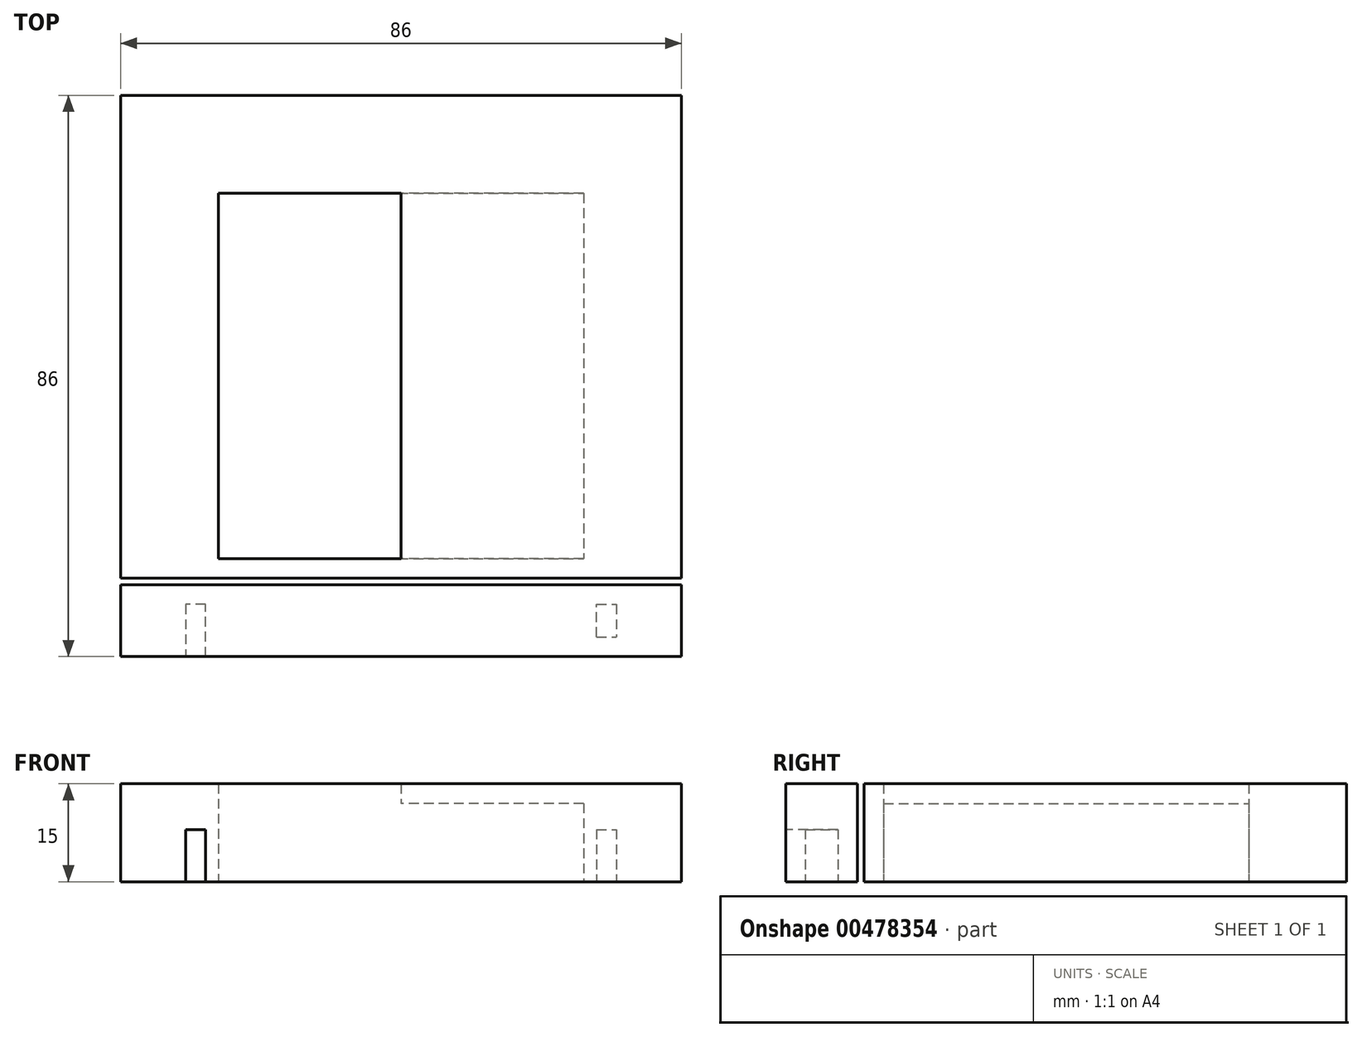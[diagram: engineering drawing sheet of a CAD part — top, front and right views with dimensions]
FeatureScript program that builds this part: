
annotation { "Feature Type Name" : "Feature", "Feature Type Description" : "" }
export const myFeature = defineFeature(function(context is Context, id is Id, definition is map)
    precondition{}
    {
        {
            var Q0;
            Q0=qCreatedBy(makeId("Top.planeOp"),FACE);
            var sketch = newSketch(context, id + "F0", { "sketchPlane" : qUnion([Q0])});
            skLineSegment(sketch, "E0", {"start": v(0, 0) * mm, "end": v(0, -43) * mm});
            skLineSegment(sketch, "E1", {"start": v(0, -43) * mm, "end": v(-43, -43) * mm});
            skLineSegment(sketch, "E2.MirrorCS", {"start": v(0, -43) * mm, "end": v(43, -43) * mm});
            skLineSegment(sketch, "E3", {"start": v(-43, -43) * mm, "end": v(-43, -32) * mm});
            skLineSegment(sketch, "E4", {"start": v(-43, -32) * mm, "end": v(0, -32) * mm});
            skLineSegment(sketch, "E5.MirrorCS", {"start": v(43, -32) * mm, "end": v(0, -32) * mm});
            skLineSegment(sketch, "E6.MirrorCS", {"start": v(43, -43) * mm, "end": v(43, -32) * mm});
            skSolve(sketch);
        }
        {
            var Q0;
            {var subQ0=sQuery(id+"F0.wireOp",EDGE,"E1");Q0=makeQuery(id+"F0.imprint","IMPRINT",FACE,{"disambiguationData":[TD([[makeQuery(id+"F0.imprint","IMPRINT",EDGE,{"derivedFrom":subQ0}),-1.0]])]});}
            var Q1;
            {var subQ0=sQuery(id+"F0.wireOp",EDGE,"E2.MirrorCS");Q1=makeQuery(id+"F0.imprint","IMPRINT",FACE,{"disambiguationData":[TD([[makeQuery(id+"F0.imprint","IMPRINT",EDGE,{"derivedFrom":subQ0}),1.0]])]});}
            extrude(context, id + "F1", {"entities" : qUnion([Q0, Q1]), "depth" : 15 * mm});
        }
        {
            var Q0;
            Q0=qCreatedBy(makeId("Top.planeOp"),FACE);
            var sketch = newSketch(context, id + "F2", { "sketchPlane" : qUnion([Q0])});
            skLineSegment(sketch, "E7", {"start": v(0, 0) * mm, "end": v(0, -43) * mm});
            skLineSegment(sketch, "E8", {"start": v(0, -43) * mm, "end": v(-30, -43) * mm});
            skLineSegment(sketch, "E9", {"start": v(-30, -43) * mm, "end": v(-30, -35) * mm});
            skLineSegment(sketch, "E10.MirrorCS", {"start": v(30, -43) * mm, "end": v(30, -35) * mm});
            skLineSegment(sketch, "E11", {"start": v(-30, -35) * mm, "end": v(-33, -35) * mm});
            skLineSegment(sketch, "E12", {"start": v(-33, -35) * mm, "end": v(-33, -43) * mm});
            skLineSegment(sketch, "E13", {"start": v(-30, -43) * mm, "end": v(-33, -43) * mm});
            skLineSegment(sketch, "E14.MirrorCS", {"start": v(33, -35) * mm, "end": v(33, -43) * mm});
            skLineSegment(sketch, "E15.MirrorCS", {"start": v(30, -43) * mm, "end": v(33, -43) * mm});
            skLineSegment(sketch, "E16.MirrorCS", {"start": v(30, -35) * mm, "end": v(33, -35) * mm});
            skLineSegment(sketch, "E17", {"start": v(-30, -43) * mm, "end": v(-30, -40) * mm});
            skLineSegment(sketch, "E18", {"start": v(-30, -40) * mm, "end": v(-33, -40) * mm});
            skLineSegment(sketch, "E19.MirrorCS", {"start": v(30, -40) * mm, "end": v(33, -40) * mm});
            skSolve(sketch);
        }
        {
            var Q0;
            Q0=makeQuery(id+"F2.imprint","IMPRINT",FACE,{"disambiguationData":[TD([[makeQuery(id+"F2.imprint","IMPRINT",EDGE,{"derivedFrom":sQuery(id+"F2.wireOp",EDGE,"E9")}),1.0]])]});
            var Q1;
            {var subQ0=sQuery(id+"F2.wireOp",EDGE,"E16.MirrorCS");Q1=makeQuery(id+"F2.imprint","IMPRINT",FACE,{"disambiguationData":[TD([[makeQuery(id+"F2.imprint","IMPRINT",EDGE,{"derivedFrom":subQ0}),-1.0]])]});}
            extrude(context, id + "F3", {"entities" : qUnion([Q0, Q1]), "operationType" : NewBodyOperationType.REMOVE, "depth" : 8 * mm});
        }
        {
            var Q0;
            Q0=qCreatedBy(makeId("Top.planeOp"),FACE);
            var sketch = newSketch(context, id + "F4", { "sketchPlane" : qUnion([Q0])});
            skLineSegment(sketch, "E20", {"start": v(0, 0) * mm, "end": v(0, 43) * mm});
            skLineSegment(sketch, "E21.bottom", {"start": v(0, 0) * mm, "end": v(-43, 0) * mm});
            skLineSegment(sketch, "E21.top", {"start": v(0, 43) * mm, "end": v(-43, 43) * mm});
            skLineSegment(sketch, "E21.right", {"start": v(-43, 0) * mm, "end": v(-43, 43) * mm});
            skLineSegment(sketch, "E22", {"start": v(-43, 0) * mm, "end": v(-43, -31) * mm});
            skLineSegment(sketch, "E23.top", {"start": v(0, -31) * mm, "end": v(-43, -31) * mm});
            skLineSegment(sketch, "E23.left", {"start": v(0, 0) * mm, "end": v(0, -31) * mm});
            skLineSegment(sketch, "E24.MirrorCS", {"start": v(0, 43) * mm, "end": v(43, 43) * mm});
            skLineSegment(sketch, "E25.MirrorCS", {"start": v(43, 0) * mm, "end": v(43, 43) * mm});
            skLineSegment(sketch, "E26.MirrorCS", {"start": v(0, -31) * mm, "end": v(43, -31) * mm});
            skLineSegment(sketch, "E27.MirrorCS", {"start": v(43, 0) * mm, "end": v(43, -31) * mm});
            skLineSegment(sketch, "E28", {"start": v(0, 0) * mm, "end": v(-28, 0) * mm});
            skLineSegment(sketch, "E29", {"start": v(-28, 0) * mm, "end": v(-28, 28) * mm});
            skLineSegment(sketch, "E30", {"start": v(-28, 28) * mm, "end": v(0, 28) * mm});
            skLineSegment(sketch, "E31.MirrorCS", {"start": v(28, 28) * mm, "end": v(0, 28) * mm});
            skLineSegment(sketch, "E32.MirrorCS", {"start": v(28, 0) * mm, "end": v(28, 28) * mm});
            skLineSegment(sketch, "E33.MirrorCS", {"start": v(-28, -28) * mm, "end": v(0, -28) * mm});
            skLineSegment(sketch, "E34.MirrorCS", {"start": v(-28, 0) * mm, "end": v(-28, -28) * mm});
            skLineSegment(sketch, "E35.MirrorCS", {"start": v(28, -28) * mm, "end": v(0, -28) * mm});
            skLineSegment(sketch, "E36.MirrorCS", {"start": v(28, 0) * mm, "end": v(28, -28) * mm});
            skSolve(sketch);
        }
        {
            var Q0;
            Q0 = qSketchRegion(id + "F4", true);
            var Q1;
            {var subQ4=sQuery(id+"F4.wireOp",EDGE,"E31.MirrorCS");Q1=makeQuery(id+"F4.imprint","IMPRINT",FACE,{"disambiguationData":[TD([[makeQuery(id+"F4.imprint","IMPRINT",EDGE,{"derivedFrom":subQ4}),1.0]])]});}
            var Q2;
            {var subQ0=sQuery(id+"F4.wireOp",EDGE,"E28");Q2=makeQuery(id+"F4.imprint","IMPRINT",FACE,{"disambiguationData":[TD([[makeQuery(id+"F4.imprint","IMPRINT",EDGE,{"derivedFrom":subQ0}),1.0]])]});}
            var Q3;
            {var subQ0=sQuery(id+"F4.wireOp",EDGE,"E28");Q3=makeQuery(id+"F4.imprint","IMPRINT",FACE,{"disambiguationData":[TD([[makeQuery(id+"F4.imprint","IMPRINT",EDGE,{"derivedFrom":subQ0}),-1.0]])]});}
            extrude(context, id + "F5", {"entities" : qUnion([Q0, Q1, Q2, Q3]), "depth" : 15 * mm});
        }
        {
            var Q0;
            {var subQ4=sQuery(id+"F4.wireOp",EDGE,"E31.MirrorCS");Q0=makeQuery(id+"F4.imprint","IMPRINT",FACE,{"disambiguationData":[TD([[makeQuery(id+"F4.imprint","IMPRINT",EDGE,{"derivedFrom":subQ4}),1.0]])]});}
            var Q1;
            {var subQ0=sQuery(id+"F4.wireOp",EDGE,"E28");Q1=makeQuery(id+"F4.imprint","IMPRINT",FACE,{"disambiguationData":[TD([[makeQuery(id+"F4.imprint","IMPRINT",EDGE,{"derivedFrom":subQ0}),-1.0]])]});}
            var Q2;
            {var subQ0=sQuery(id+"F4.wireOp",EDGE,"E28");Q2=makeQuery(id+"F4.imprint","IMPRINT",FACE,{"disambiguationData":[TD([[makeQuery(id+"F4.imprint","IMPRINT",EDGE,{"derivedFrom":subQ0}),1.0]])]});}
            extrude(context, id + "F6", {"entities" : qUnion([Q0, Q1, Q2]), "operationType" : NewBodyOperationType.REMOVE, "depth" : 12 * mm});
        }
        {
            var Q0;
            Q0=makeQuery(id+"F1.opExtrude","SWEPT_BODY",BODY,{"disambiguationData":[OSD([sQuery(id+"F0.wireOp",EDGE,"E1"),sQuery(id+"F0.wireOp",EDGE,"E2.MirrorCS"),sQuery(id+"F0.wireOp",EDGE,"E3"),sQuery(id+"F0.wireOp",EDGE,"E4"),sQuery(id+"F0.wireOp",EDGE,"E5.MirrorCS"),sQuery(id+"F0.wireOp",EDGE,"E6.MirrorCS")])]});
            var Q1;
            Q1=makeQuery(id+"F5.opExtrude","SWEPT_BODY",BODY,{"disambiguationData":[OSD([sQuery(id+"F4.wireOp",EDGE,"E21.top"),sQuery(id+"F4.wireOp",EDGE,"E21.right"),sQuery(id+"F4.wireOp",EDGE,"E23.top"),sQuery(id+"F4.wireOp",EDGE,"E22"),sQuery(id+"F4.wireOp",EDGE,"E24.MirrorCS"),sQuery(id+"F4.wireOp",EDGE,"E25.MirrorCS"),sQuery(id+"F4.wireOp",EDGE,"E26.MirrorCS"),sQuery(id+"F4.wireOp",EDGE,"E27.MirrorCS")])]});
            var Q2;
            Q2=qCreatedBy(makeId("Origin.pointOp"),VERTEX);
            var Q3;
            Q3=qCreatedBy(makeId("Top.planeOp"),FACE);
            transform(context, id + "F7", {"entities" : qUnion([Q0, Q1]), "transformType" : TransformType.TRANSLATION_DISTANCE, "transformDirection" : qUnion([Q3]), "distance" : 43 * mm, "makeCopy" : false});
        }
    });
